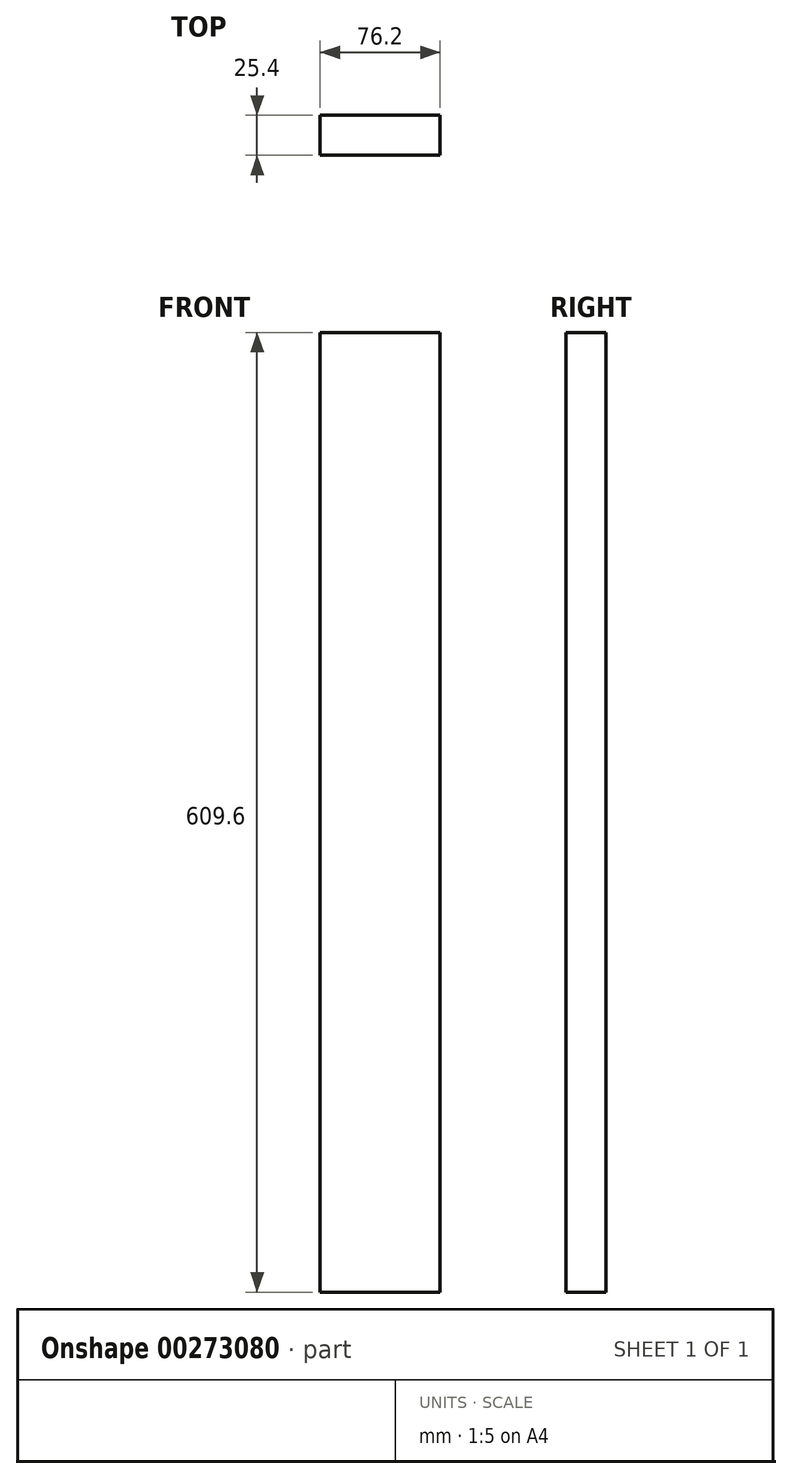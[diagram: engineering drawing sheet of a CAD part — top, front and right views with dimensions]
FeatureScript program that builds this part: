
annotation { "Feature Type Name" : "Feature", "Feature Type Description" : "" }
export const myFeature = defineFeature(function(context is Context, id is Id, definition is map)
    precondition{}
    {
        {
            var Q0;
            Q0=qCreatedBy(makeId("Front.planeOp"),FACE);
            var sketch = newSketch(context, id + "F0", { "sketchPlane" : qUnion([Q0])});
            skLineSegment(sketch, "E0.bottom", {"start": v(-96.08, 305.7) * mm, "end": v(-19.88, 305.7) * mm});
            skLineSegment(sketch, "E0.top", {"start": v(-96.08, -303.9) * mm, "end": v(-19.88, -303.9) * mm});
            skLineSegment(sketch, "E0.left", {"start": v(-96.08, 305.7) * mm, "end": v(-96.08, -303.9) * mm});
            skLineSegment(sketch, "E0.right", {"start": v(-19.88, 305.7) * mm, "end": v(-19.88, -303.9) * mm});
            skSolve(sketch);
        }
        {
            var Q0;
            Q0 = qSketchRegion(id + "F0", true);
            extrude(context, id + "F1", {"entities" : qUnion([Q0]), "depth" : 25.4 * mm});
        }
    });
